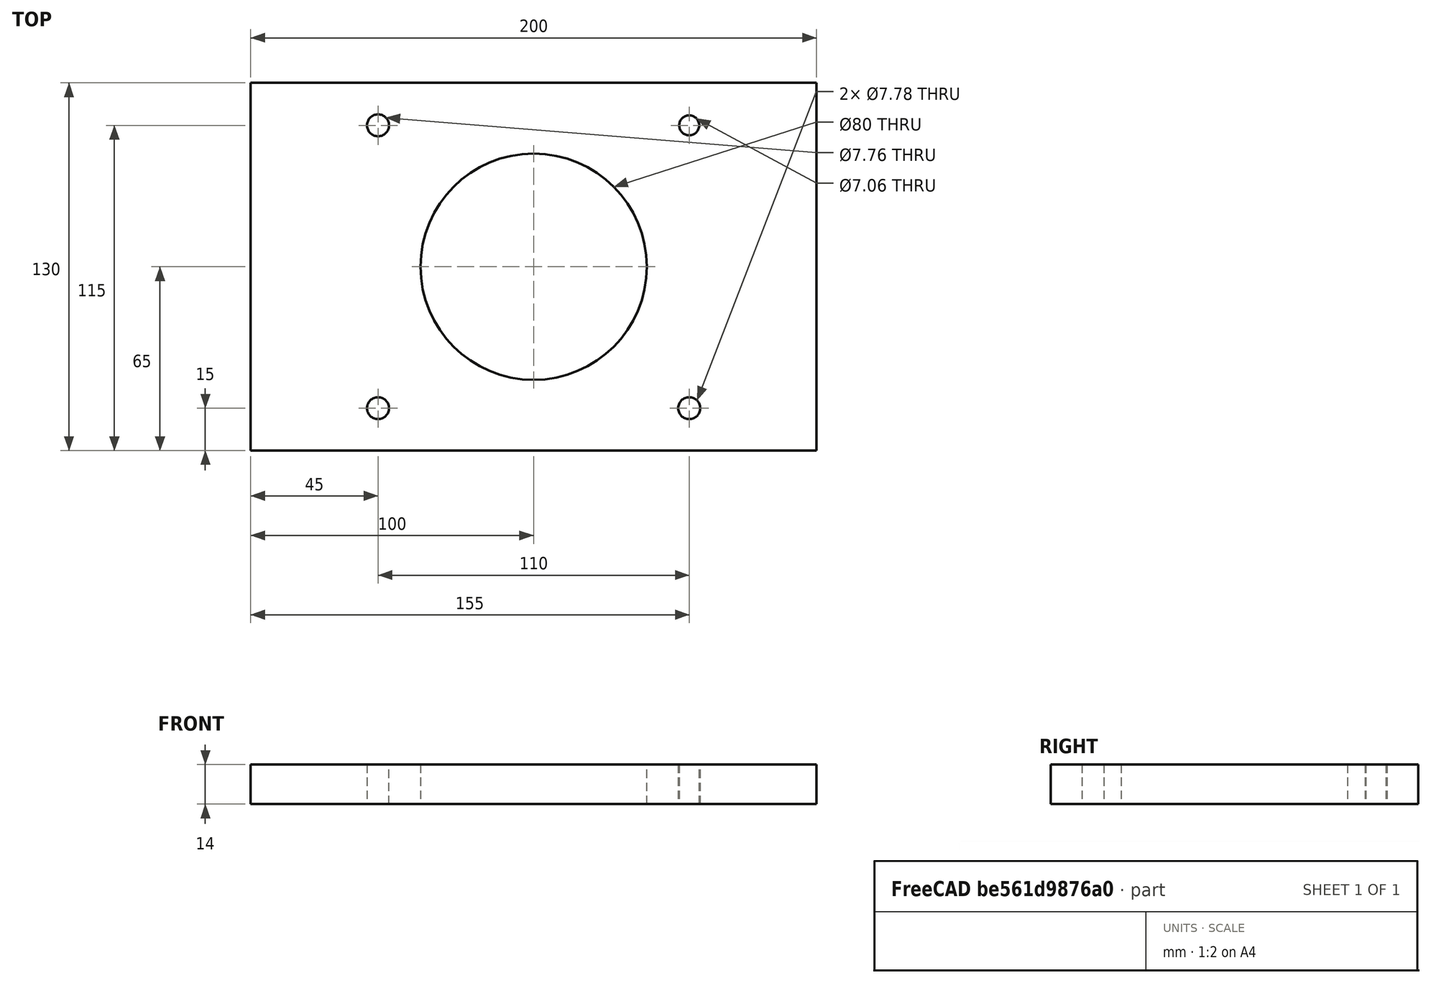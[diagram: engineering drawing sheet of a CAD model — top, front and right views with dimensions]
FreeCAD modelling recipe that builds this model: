
FCSTD DOCUMENT  (FreeCAD 0.19R24276 (Git))
Label: Plate_200x130_d80_4napravl
License: All rights reserved
LicenseURL: http://en.wikipedia.org/wiki/All_rights_reserved
objects: Sketcher::SketchObject×1, PartDesign::Pad×1, PartDesign::Body×1
note: 4 computed .brp shape members not serialized (recipe doc carries the construction recipe); baked Part::Feature solids carry a one-line shape summary decoded from their .brp

FEATURE [Sketcher::SketchObject] Sketch
  FullyConstrained = false
  MapMode = 5
  Support = -> [XY_Plane]
  sketch-geometry (13):
    g0: LineSegment StartX=0 StartY=0 StartZ=0 EndX=200 EndY=0 EndZ=0
    g1: LineSegment StartX=200 StartY=0 StartZ=0 EndX=200 EndY=130 EndZ=0
    g2: LineSegment StartX=200 StartY=130 StartZ=0 EndX=0 EndY=130 EndZ=0
    g3: LineSegment StartX=0 StartY=130 StartZ=0 EndX=0 EndY=0 EndZ=0
    g4: Circle CenterX=100 CenterY=65 CenterZ=0 NormalX=0 NormalY=0 NormalZ=1 AngleXU=0 Radius=40
    g5: Circle CenterX=45 CenterY=115 CenterZ=0 NormalX=0 NormalY=0 NormalZ=1 AngleXU=0 Radius=3.88065
    g6: Circle CenterX=45 CenterY=15 CenterZ=0 NormalX=0 NormalY=0 NormalZ=1 AngleXU=0 Radius=3.88852
    g7: Circle CenterX=155 CenterY=115 CenterZ=0 NormalX=0 NormalY=0 NormalZ=1 AngleXU=0 Radius=3.52808
    g8: Circle CenterX=155 CenterY=15 CenterZ=0 NormalX=0 NormalY=0 NormalZ=1 AngleXU=0 Radius=3.88853
    g9: LineSegment StartX=45 StartY=15 StartZ=0 EndX=45 EndY=115 EndZ=0
    g10: LineSegment StartX=45 StartY=15 StartZ=0 EndX=155 EndY=15 EndZ=0
    g11: LineSegment StartX=155 StartY=115 StartZ=0 EndX=155 EndY=15 EndZ=0
    g12: LineSegment StartX=45 StartY=115 StartZ=0 EndX=155 EndY=115 EndZ=0
  constraints (28):
    c: Coincident(g0,g1)
    c: Coincident(g1,g2)
    c: Coincident(g2,g3)
    c: Coincident(g3,g0)
    c: Horizontal(g0)
    c: Horizontal(g2)
    c: Vertical(g1)
    c: Vertical(g3)
    c: Coincident(g0,g-1)
    c: DistanceY(g1,g1) = 130
    c: DistanceX(g0,g0) = 200
    c: Symmetric(g2,g0,g4)
    c: Diameter(g4) = 80
    c: DistanceX(g0,g6) = 45
    c: Coincident(g9,g6)
    c: Coincident(g9,g5)
    c: Vertical(g9)
    c: Coincident(g10,g6)
    c: Coincident(g10,g8)
    c: Horizontal(g10)
    c: Coincident(g11,g7)
    c: Coincident(g11,g8)
    c: Vertical(g11)
    c: Coincident(g12,g5)
    c: Coincident(g12,g7)
    c: Horizontal(g12)
    c: Symmetric(g7,g6,g4)
    c: DistanceY(g0,g6) = 15
FEATURE [PartDesign::Pad] Pad
  Direction = (1,1,1)
  Length = 14
  Length2 = 100
  Profile = -> Sketch
  Type = 0
FEATURE [PartDesign::Body] Body
  Group = -> [Sketch,Pad]
  Origin = -> Origin
  Tip = -> Pad
